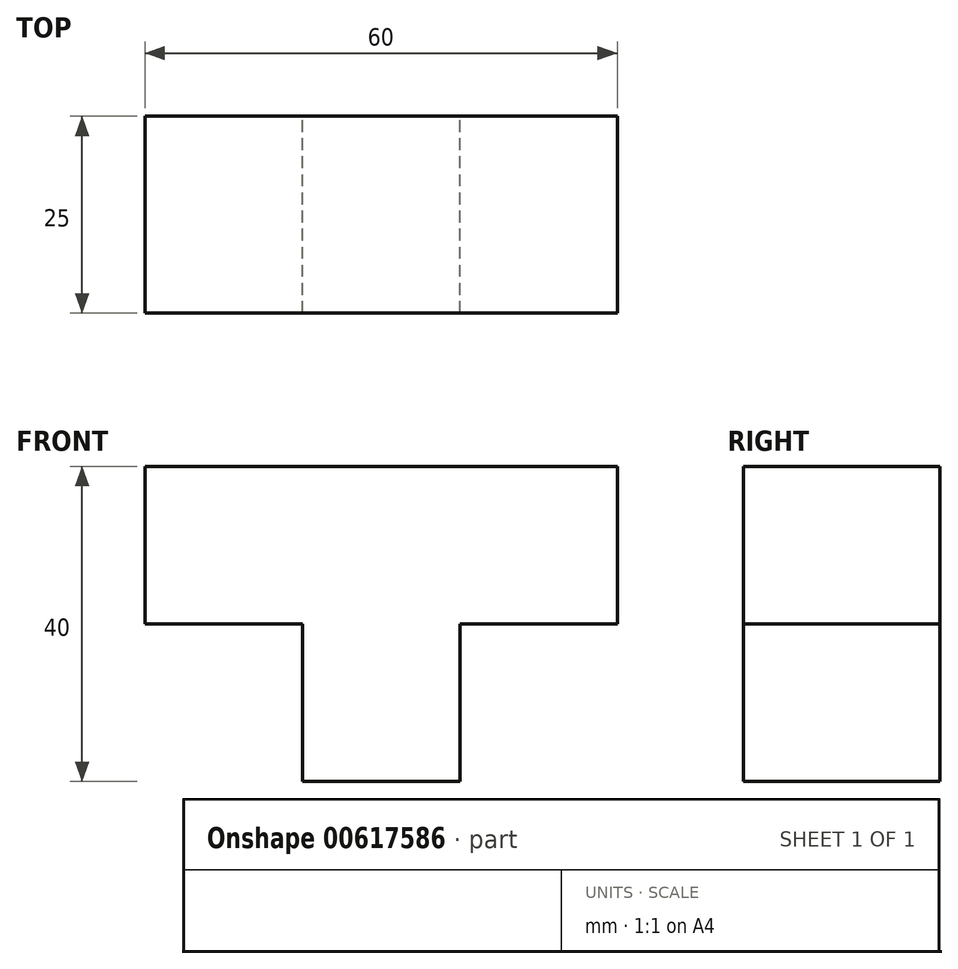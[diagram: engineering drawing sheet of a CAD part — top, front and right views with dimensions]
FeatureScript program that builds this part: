
annotation { "Feature Type Name" : "Feature", "Feature Type Description" : "" }
export const myFeature = defineFeature(function(context is Context, id is Id, definition is map)
    precondition{}
    {
        {
            var Q0;
            Q0=qCreatedBy(makeId("Front.planeOp"),FACE);
            var sketch = newSketch(context, id + "F0", { "sketchPlane" : qUnion([Q0])});
            skLineSegment(sketch, "E0", {"start": v(0, 0) * mm, "end": v(-20, 0) * mm});
            skLineSegment(sketch, "E1", {"start": v(-20, 0) * mm, "end": v(-20, -20) * mm});
            skLineSegment(sketch, "E2", {"start": v(-20, -20) * mm, "end": v(0, -20) * mm});
            skLineSegment(sketch, "E3", {"start": v(0, -20) * mm, "end": v(0, 0) * mm});
            skLineSegment(sketch, "E4", {"start": v(0, 0) * mm, "end": v(20, 0) * mm});
            skLineSegment(sketch, "E5", {"start": v(20, 0) * mm, "end": v(20, -20) * mm});
            skLineSegment(sketch, "E6", {"start": v(20, -20) * mm, "end": v(0, -20) * mm});
            skLineSegment(sketch, "E7", {"start": v(20, -20) * mm, "end": v(40, -20) * mm});
            skLineSegment(sketch, "E8", {"start": v(40, -20) * mm, "end": v(40, 0) * mm});
            skLineSegment(sketch, "E9", {"start": v(40, 0) * mm, "end": v(20, 0) * mm});
            skLineSegment(sketch, "E10", {"start": v(0, -20) * mm, "end": v(0, -40) * mm});
            skLineSegment(sketch, "E11", {"start": v(0, -40) * mm, "end": v(20, -40) * mm});
            skLineSegment(sketch, "E12", {"start": v(20, -40) * mm, "end": v(20, -20) * mm});
            skSolve(sketch);
        }
        {
            var Q0;
            Q0 = qSketchRegion(id + "F0", true);
            extrude(context, id + "F1", {"entities" : qUnion([Q0]), "depth" : 25 * mm, "offsetDistance" : 25 * mm});
        }
    });
